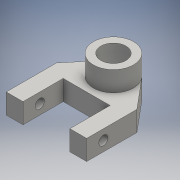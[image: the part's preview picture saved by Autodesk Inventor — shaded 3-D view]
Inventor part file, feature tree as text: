
AUTODESK INVENTOR PART (.ipt)
format: ipt  version: 2016 (Build 200138000, 138)  size: 133,120 bytes
history: native  units: mm
features: extrude x3, sketch x3, projected_geometry x1
ambient origin geometry x8: Origin, YZ Plane, XZ Plane, XY Plane, X Axis, Y Axis, Z Axis, Center Point
bodies: Solid1 (feature_tree)
feature tree (7):
  extrude  "Extrusion1"  Depth=10.0mm
  extrude  "Extrusion2"  Depth=24.0mm
  extrude  "Extrusion3"  Depth=12.0mm
  sketch  "Sketch1"  dims[d0=28.0mm d1=10.0mm]
  sketch  "Sketch2"  dims[d2=24.0mm d3=40.0mm]
  projected_geometry  "Projected Loop1"
  sketch  "Sketch3"  dims[d4=30.0mm d5=15.0mm d6=12.0mm d7=12.0mm d8=0.0mm d9=10.0mm d10=5.5mm d11=12.0mm d12=0.0mm d13=12.0mm d14=0.0mm]
